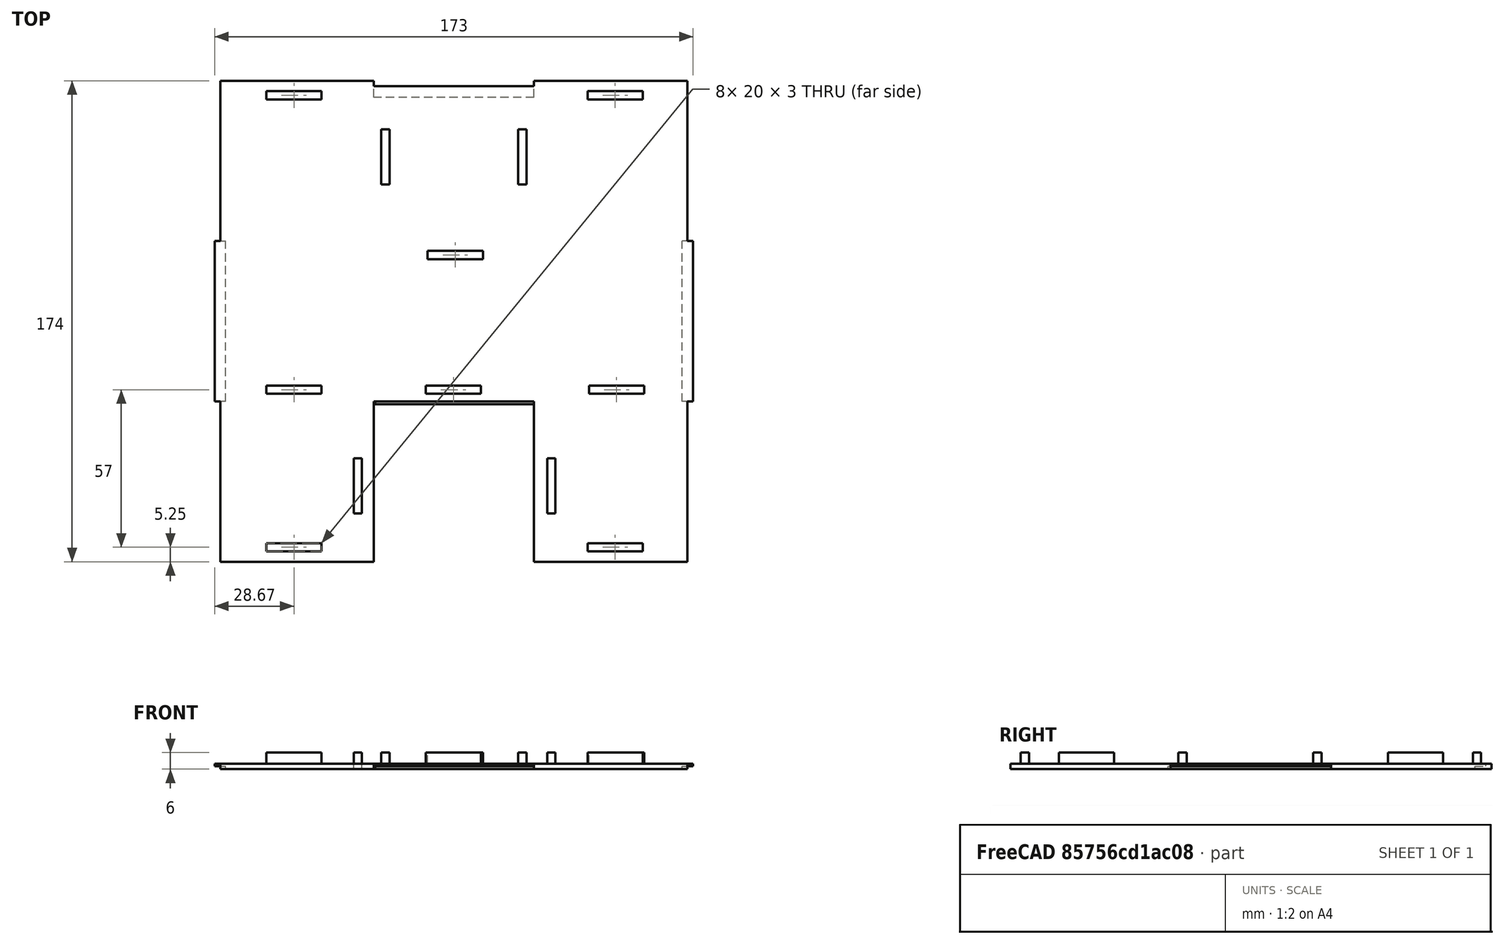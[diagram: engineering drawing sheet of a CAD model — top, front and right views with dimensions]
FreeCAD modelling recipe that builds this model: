
FCSTD DOCUMENT  (FreeCAD 0.21R33694 (Git))
Label: maze_cover_B_v4
License: All rights reserved
LicenseURL: https://en.wikipedia.org/wiki/All_rights_reserved
objects: Part::Box×23, Part::MultiFuse×1
note: 24 computed .brp shape members not serialized (recipe doc carries the construction recipe); baked Part::Feature solids carry a one-line shape summary decoded from their .brp

FEATURE [Part::Box] Box  label="Cube"
  AttacherType = Attacher::AttachEngine3D
  Height = 2
  Length = 165
  Placement = pos=(4,0,0) rot=(0,0,1;0rad)
  Width = 58
FEATURE [Part::Box] Box001  label="Cube001"
  AttacherType = Attacher::AttachEngine3D
  Height = 2
  Length = 110
  Placement = pos=(115.5,0,0) rot=(0,0,1;1.5708rad)
  Width = 58
FEATURE [Part::Box] Box002  label="Cube002"
  AttacherType = Attacher::AttachEngine3D
  Height = 6
  Length = 20
  Placement = pos=(18.67,-54.25,0) rot=(0,0,1;0rad)
  Width = 3
FEATURE [Part::Box] Box003  label="Cube003"
  AttacherType = Attacher::AttachEngine3D
  Height = 6
  Length = 20
  Placement = pos=(76.34,2.75,0) rot=(0,0,1;0rad)
  Width = 3
FEATURE [Part::Box] Box004  label="Cube004"
  AttacherType = Attacher::AttachEngine3D
  Height = 6
  Length = 20
  Placement = pos=(134.83,-54.25,0) rot=(0,0,1;0rad)
  Width = 3
FEATURE [Part::Box] Box007  label="Cube007"
  AttacherType = Attacher::AttachEngine3D
  Height = 6
  Length = 20
  Placement = pos=(63.25,78.5,0) rot=(0,0,1;1.5708rad)
  Width = 3
FEATURE [Part::Box] Box008  label="Cube008"
  AttacherType = Attacher::AttachEngine3D
  Height = 6
  Length = 20
  Placement = pos=(112.75,78.5,0) rot=(0,0,1;1.5708rad)
  Width = 3
FEATURE [Part::Box] Box009  label="Cube009"
  AttacherType = Attacher::AttachEngine3D
  Height = 1
  Length = 4
  Placement = pos=(0,0,1) rot=(0,0,1;0rad)
  Width = 58
FEATURE [Part::Box] Box010  label="Cube010"
  AttacherType = Attacher::AttachEngine3D
  Height = 1
  Length = 4
  Placement = pos=(169,0,1) rot=(0,0,1;0rad)
  Width = 58
FEATURE [Part::Box] Box011  label="Cube011"
  AttacherType = Attacher::AttachEngine3D
  Height = 1
  Length = 4
  Placement = pos=(115.5,110,1) rot=(0,0,1;1.5708rad)
  Width = 58
FEATURE [Part::Box] Box012  label="Cube012"
  AttacherType = Attacher::AttachEngine3D
  Height = 2
  Length = 58
  Placement = pos=(57.5,58,0) rot=(0,0,1;1.5708rad)
  Width = 55.5
FEATURE [Part::Box] Box017  label="Cube017"
  AttacherType = Attacher::AttachEngine3D
  Height = 6
  Length = 20
  Placement = pos=(18.67,2.75,0) rot=(0,0,1;0rad)
  Width = 3
FEATURE [Part::Box] Box018  label="Cube018"
  AttacherType = Attacher::AttachEngine3D
  Height = 6
  Length = 20
  Placement = pos=(135.333,2.75,0) rot=(0,0,1;0rad)
  Width = 3
FEATURE [Part::Box] Box026  label="Cube026"
  AttacherType = Attacher::AttachEngine3D
  Height = 6
  Length = 20
  Placement = pos=(77,51.5,0) rot=(0,0,1;0rad)
  Width = 3
FEATURE [Part::Box] Box027  label="Cube027"
  AttacherType = Attacher::AttachEngine3D
  Height = 1
  Length = 58
  Placement = pos=(58,-1,0) rot=(0,0,1;0rad)
  Width = 3
FEATURE [Part::Box] Box029  label="Cube029"
  AttacherType = Attacher::AttachEngine3D
  Height = 6
  Length = 20
  Placement = pos=(18.67,109.25,0) rot=(0,0,1;0rad)
  Width = 3
FEATURE [Part::Box] Box030  label="Cube030"
  AttacherType = Attacher::AttachEngine3D
  Height = 2
  Length = 58
  Placement = pos=(171,58,0) rot=(0,0,1;1.5708rad)
  Width = 55.5
FEATURE [Part::Box] Box006  label="Cube006"
  AttacherType = Attacher::AttachEngine3D
  Height = 6
  Length = 20
  Placement = pos=(134.83,109.25,0) rot=(0,0,1;0rad)
  Width = 3
FEATURE [Part::Box] Box031  label="Cube031"
  AttacherType = Attacher::AttachEngine3D
  Height = 2
  Length = 58
  Placement = pos=(57.5,-58,0) rot=(0,0,1;1.5708rad)
  Width = 55.5
FEATURE [Part::Box] Box032  label="Cube032"
  AttacherType = Attacher::AttachEngine3D
  Height = 2
  Length = 58
  Placement = pos=(171,-58,0) rot=(0,0,1;1.5708rad)
  Width = 55.5
FEATURE [Part::Box] Box033  label="Cube033"
  AttacherType = Attacher::AttachEngine3D
  Height = 6
  Length = 20
  Placement = pos=(53.25,-40.5,0) rot=(0,0,1;1.5708rad)
  Width = 3
FEATURE [Part::Box] Box034  label="Cube034"
  AttacherType = Attacher::AttachEngine3D
  Height = 6
  Length = 20
  Placement = pos=(53.25,-40.5,0) rot=(0,0,1;1.5708rad)
  Width = 3
FEATURE [Part::Box] Box035  label="Cube035"
  AttacherType = Attacher::AttachEngine3D
  Height = 6
  Length = 20
  Placement = pos=(123.25,-40.5,0) rot=(0,0,1;1.5708rad)
  Width = 3
FEATURE [Part::MultiFuse] Fusion
  Shapes = -> [Box,Box001,Box002,Box003,Box004,Box006,Box007,Box008,Box009,Box010,Box012,Box011,Box017,Box018,Box026,Box027,Box029,Box030,Box031,Box032,Box033,Box035]
